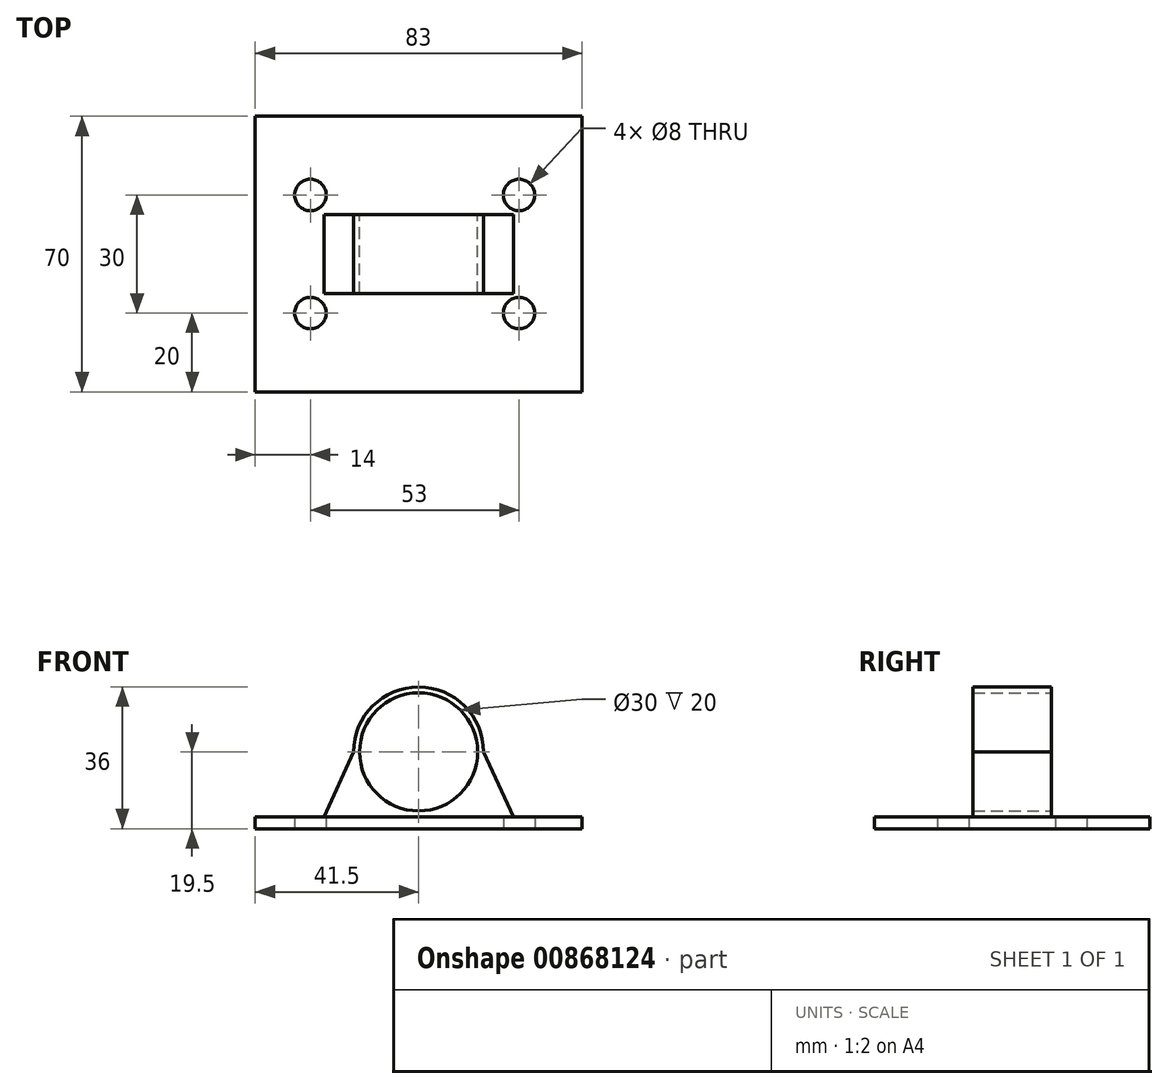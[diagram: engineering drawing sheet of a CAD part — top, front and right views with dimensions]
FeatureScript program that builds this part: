
annotation { "Feature Type Name" : "Feature", "Feature Type Description" : "" }
export const myFeature = defineFeature(function(context is Context, id is Id, definition is map)
    precondition{}
    {
        {
            var Q0;
            Q0=qCreatedBy(makeId("Top.planeOp"),FACE);
            var sketch = newSketch(context, id + "F0", { "sketchPlane" : qUnion([Q0])});
            skLineSegment(sketch, "E0.bottom", {"start": v(41.5, 35) * mm, "end": v(-41.5, 35) * mm});
            skLineSegment(sketch, "E0.top", {"start": v(41.5, -35) * mm, "end": v(-41.5, -35) * mm});
            skLineSegment(sketch, "E0.left", {"start": v(41.5, 35) * mm, "end": v(41.5, -35) * mm});
            skLineSegment(sketch, "E0.right", {"start": v(-41.5, 35) * mm, "end": v(-41.5, -35) * mm});
            skPoint(sketch, "E0.middle", {"position": v(0, 0) * mm});
            skSolve(sketch);
        }
        {
            var Q0;
            Q0=makeQuery(id+"F0.imprint","IMPRINT",FACE,{"disambiguationData":[TD([[makeQuery(id+"F0.imprint","IMPRINT",EDGE,{"derivedFrom":sQuery(id+"F0.wireOp",EDGE,"E0.bottom")}),1.0]])]});
            extrude(context, id + "F1", {"entities" : qUnion([Q0]), "oppositeDirection" : true, "depth" : 3 * mm, "offsetDistance" : 25 * mm});
        }
        {
            var Q0;
            Q0=qCreatedBy(makeId("Front.planeOp"),FACE);
            var sketch = newSketch(context, id + "F2", { "sketchPlane" : qUnion([Q0])});
            skCircle(sketch, "E1", {"center": v(0, 16.5) * mm, "radius": 15 * mm});
            skCircle(sketch, "E2", {"center": v(0, 16.5) * mm, "radius": 16.5 * mm});
            skLineSegment(sketch, "E3", {"start": v(-16.5, 16.5) * mm, "end": v(-24.06, 0) * mm});
            skLineSegment(sketch, "E4", {"start": v(16.5, 16.5) * mm, "end": v(24.06, 0) * mm});
            skLineSegment(sketch, "E5", {"start": v(-24.06, 0) * mm, "end": v(24.06, 0) * mm});
            skSolve(sketch);
        }
        {
            var Q0;
            {var subQ0=sQuery(id+"F2.wireOp",EDGE,"E3");Q0=makeQuery(id+"F2.imprint","IMPRINT",FACE,{"disambiguationData":[TD([[makeQuery(id+"F2.imprint","IMPRINT",EDGE,{"derivedFrom":subQ0}),1.0]])]});}
            var Q1;
            {var subQ0=sQuery(id+"F2.wireOp",EDGE,"E4");Q1=makeQuery(id+"F2.imprint","IMPRINT",FACE,{"disambiguationData":[TD([[makeQuery(id+"F2.imprint","IMPRINT",EDGE,{"derivedFrom":subQ0}),-1.0]])]});}
            var Q2;
            Q2=makeQuery(id+"F2.imprint","IMPRINT",FACE,{"disambiguationData":[TD([[makeQuery(id+"F2.imprint","IMPRINT",EDGE,{"derivedFrom":sQuery(id+"F2.wireOp",EDGE,"E1")}),-1.0]])]});
            extrude(context, id + "F3", {"entities" : qUnion([Q0, Q1, Q2]), "operationType" : NewBodyOperationType.ADD, "endBound" : BoundingType.SYMMETRIC, "depth" : 20 * mm, "offsetDistance" : 25 * mm});
        }
        {
            var Q0;
            Q0=makeQuery(id+"F1.opExtrude","CAP_FACE",FACE,{"disambiguationData":[OSD([sQuery(id+"F0.wireOp",EDGE,"E0.bottom"),sQuery(id+"F0.wireOp",EDGE,"E0.top"),sQuery(id+"F0.wireOp",EDGE,"E0.left"),sQuery(id+"F0.wireOp",EDGE,"E0.right")])],"isStart":false});
            var sketch = newSketch(context, id + "F4", { "sketchPlane" : qUnion([Q0])});
            skLineSegment(sketch, "E6", {"start": v(-41.5, -35) * mm, "end": v(41.5, 35) * mm, "construction": true});
            skLineSegment(sketch, "E7", {"start": v(41.5, -35) * mm, "end": v(-41.5, 35) * mm, "construction": true});
            skLineSegment(sketch, "E8", {"start": v(-41.5, 0) * mm, "end": v(41.5, 0) * mm, "construction": true});
            skLineSegment(sketch, "E9", {"start": v(0, -35) * mm, "end": v(0, 35) * mm, "construction": true});
            skCircle(sketch, "E10", {"center": v(-27.5, -15) * mm, "radius": 4 * mm});
            skCircle(sketch, "E11.0.1.0", {"center": v(-27.5, 15) * mm, "radius": 4 * mm});
            skCircle(sketch, "E11.1.0.0", {"center": v(25.5, -15) * mm, "radius": 4 * mm});
            skCircle(sketch, "E11.1.1.0", {"center": v(25.5, 15) * mm, "radius": 4 * mm});
            skLineSegment(sketch, "E11.direction1", {"start": v(-27.5, -15) * mm, "end": v(25.5, -15) * mm, "construction": true});
            skLineSegment(sketch, "E11.direction2", {"start": v(-27.5, -15) * mm, "end": v(-27.5, 15) * mm, "construction": true});
            skLineSegment(sketch, "E12", {"start": v(0, 0) * mm, "end": v(-41.5, -13.2) * mm, "construction": true});
            skLineSegment(sketch, "E13", {"start": v(0, 0) * mm, "end": v(41.5, 13.2) * mm, "construction": true});
            skLineSegment(sketch, "E14", {"start": v(0, 0) * mm, "end": v(-41.5, 13.2) * mm, "construction": true});
            skLineSegment(sketch, "E15", {"start": v(0, 0) * mm, "end": v(41.5, -17.19) * mm, "construction": true});
            skSolve(sketch);
        }
        {
            var Q0;
            Q0=makeQuery(id+"F4.imprint","IMPRINT",FACE,{"disambiguationData":[TD([[makeQuery(id+"F4.imprint","IMPRINT",EDGE,{"derivedFrom":sQuery(id+"F4.wireOp",EDGE,"E10")}),1.0]])]});
            var Q1;
            Q1=makeQuery(id+"F4.imprint","IMPRINT",FACE,{"disambiguationData":[TD([[makeQuery(id+"F4.imprint","IMPRINT",EDGE,{"derivedFrom":sQuery(id+"F4.wireOp",EDGE,"E11.0.1.0")}),1.0]])]});
            var Q2;
            Q2=makeQuery(id+"F4.imprint","IMPRINT",FACE,{"disambiguationData":[TD([[makeQuery(id+"F4.imprint","IMPRINT",EDGE,{"derivedFrom":sQuery(id+"F4.wireOp",EDGE,"E11.1.1.0")}),1.0]])]});
            var Q3;
            Q3=makeQuery(id+"F4.imprint","IMPRINT",FACE,{"disambiguationData":[TD([[makeQuery(id+"F4.imprint","IMPRINT",EDGE,{"derivedFrom":sQuery(id+"F4.wireOp",EDGE,"E11.1.0.0")}),1.0]])]});
            extrude(context, id + "F5", {"entities" : qUnion([Q0, Q1, Q2, Q3]), "operationType" : NewBodyOperationType.REMOVE, "oppositeDirection" : true, "depth" : 25 * mm, "offsetDistance" : 25 * mm});
        }
    });
